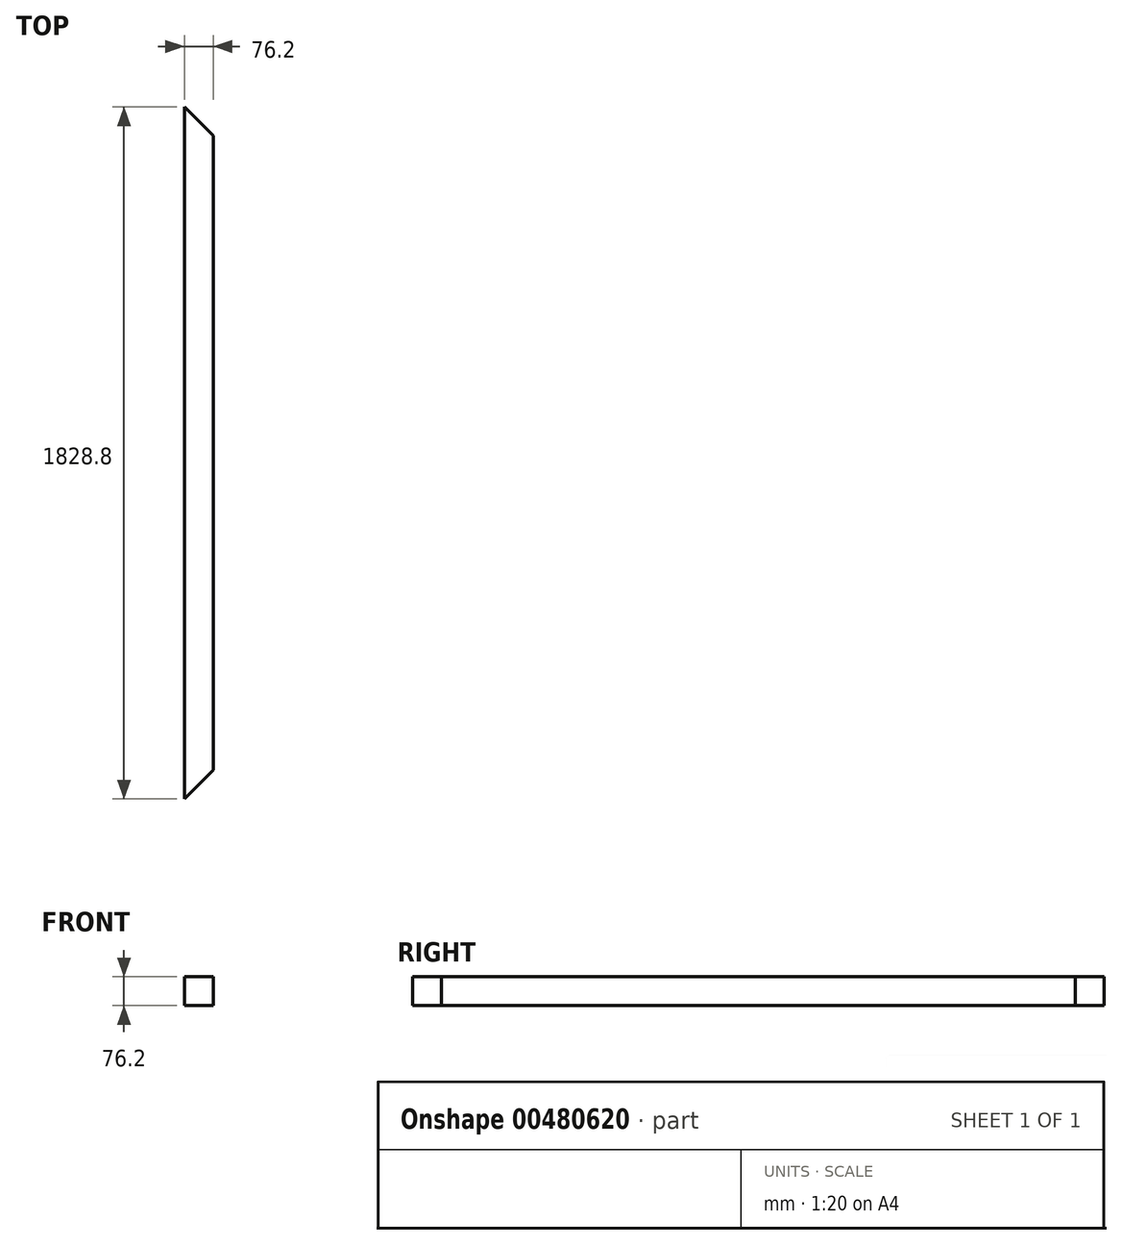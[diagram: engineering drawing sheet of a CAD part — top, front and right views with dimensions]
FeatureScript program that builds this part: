
annotation { "Feature Type Name" : "Feature", "Feature Type Description" : "" }
export const myFeature = defineFeature(function(context is Context, id is Id, definition is map)
    precondition{}
    {
        {
            var Q0;
            Q0=qCreatedBy(makeId("Top.planeOp"),FACE);
            var sketch = newSketch(context, id + "F0", { "sketchPlane" : qUnion([Q0])});
            skLineSegment(sketch, "E0.left", {"start": v(38.1, 838.2) * mm, "end": v(38.1, -838.2) * mm});
            skLineSegment(sketch, "E0.right", {"start": v(-38.1, 914.4) * mm, "end": v(-38.1, -914.4) * mm});
            skPoint(sketch, "E0.middle", {"position": v(0, 0) * mm});
            skLineSegment(sketch, "E1", {"start": v(-38.1, -914.4) * mm, "end": v(38.1, -838.2) * mm});
            skLineSegment(sketch, "E2", {"start": v(-38.1, 914.4) * mm, "end": v(38.1, 838.2) * mm});
            skPoint(sketch, "E0.top.start.orphan", {"position": v(38.1, -914.4) * mm});
            skPoint(sketch, "E3.orphan", {"position": v(38.1, 914.4) * mm});
            skSolve(sketch);
        }
        {
            var Q0;
            Q0 = qSketchRegion(id + "F0", true);
            extrude(context, id + "F1", {"entities" : qUnion([Q0]), "depth" : 76.2 * mm});
        }
    });
